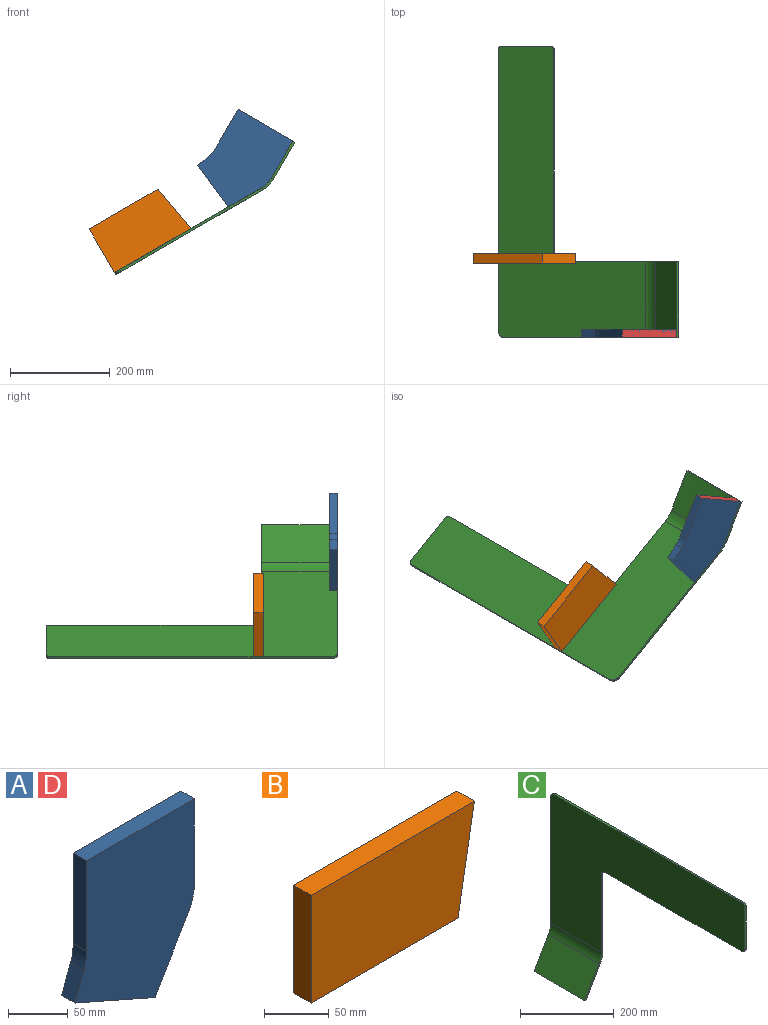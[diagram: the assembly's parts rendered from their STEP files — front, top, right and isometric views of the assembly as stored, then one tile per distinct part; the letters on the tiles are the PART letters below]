
ASSEMBLY  parts=4 mates=9
PART A: 11 faces, bbox 140.6x15.9x179.9 mm
  f0: plane 179.9x140.62mm, normal (0,-1,0), area 19853.6mm2, adj f2,f3,f4,f5,f6,f7,f8,f9
  f1: plane 179.9x140.62mm, normal (0,1,0), area 19853.6mm2, adj f2,f3,f4,f5,f6,f7,f8,f9
  f2: plane 92.5x15.88mm, normal (-1,0,0), area 1468.4mm2, adj f0,f1,f4,f10
  f3: plane 89.68x15.88mm, normal (1,0,0), area 1423.6mm2, adj f0,f1,f4,f5
  f4: plane 127x15.88mm, normal (0,0,1), area 2016.1mm2, adj f0,f1,f2,f3
  f5: cylinder r=42.03mm len=15.88mm, axis (0,-1,0), area 193.9mm2, adj f0,f1,f3,f7
  f6: plane 67.98x39.7mm, normal (0.86,0,-0.5), area 1249.7mm2, adj f0,f1,f7,f9
  f7: cylinder r=40.32mm len=15.88mm, axis (0,-1,0), area 177.7mm2, adj f0,f1,f5,f6
  f8: plane 28.24x15.88mm, normal (-0.94,0,0.35), area 478.1mm2, adj f0,f1,f9,f10
  f9: plane 94.25x41.52mm, normal (-0.4,0,-0.92), area 1635mm2, adj f0,f1,f6,f8
  f10: cylinder r=50.8mm len=17.64mm, axis (0,1,0), area 286mm2, adj f0,f1,f2,f8
PART B: 6 faces, bbox 177.8x19.1x101.6 mm
  f0: plane 101.6x19.05mm, normal (-1,0,0), area 1935.5mm2, adj f1,f3,f4,f5
  f1: plane 159.89x19.05mm, normal (0,0,-1), area 3045.8mm2, adj f0,f2,f4,f5
  f2: plane 101.6x19.05mm, normal (0.98,0,-0.17), area 1965.3mm2, adj f1,f3,f4,f5
  f3: plane 177.8x19.05mm, normal (0,0,1), area 3387.1mm2, adj f0,f2,f4,f5
  f4: plane 177.8x101.6mm, normal (0,-1,0), area 17154.4mm2, adj f0,f1,f2,f3
  f5: plane 177.8x101.6mm, normal (0,1,0), area 17154.4mm2, adj f0,f1,f2,f3
PART C: 20 faces, bbox 54.9x584.2x444.9 mm
  f0: plane 565.15x4.76mm, normal (0,0,1), area 2691.5mm2, adj f1,f8,f9,f10
  f1: cylinder r=12.7mm len=12.7mm, axis (1,0,0), area 95mm2, adj f0,f2,f9,f10
  f2: plane 329.29x4.76mm, normal (0,1,0), area 1568.2mm2, adj f1,f9,f10,f16
  f3: plane 202.29x4.76mm, normal (0,-1,0), area 963.4mm2, adj f4,f9,f10,f17
  f4: cylinder r=12.7mm len=12.7mm, axis (1,0,0), area 95mm2, adj f3,f5,f9,f10
  f5: plane 412.75x4.76mm, normal (0,0,-1), area 1965.7mm2, adj f4,f6,f9,f10
  f6: cylinder r=6.35mm len=6.35mm, axis (1,0,0), area 47.5mm2, adj f5,f7,f9,f10
  f7: plane 114.3x4.76mm, normal (0,-1,0), area 544.4mm2, adj f6,f8,f9,f10
  f8: cylinder r=6.35mm len=6.35mm, axis (1,0,0), area 47.5mm2, adj f0,f7,f9,f10
  f9: plane 584.2x341.99mm, normal (-1,0,0), area 106940.3mm2, adj f0,f1,f2,f3,f4,f5,f6,f7
  f10: plane 584.2x341.99mm, normal (1,0,0), area 106940.3mm2, adj f0,f1,f2,f3,f4,f5,f6,f7
  f11: plane 77.48x47.48mm, normal (0,-1,0), area 413mm2, adj f13,f14,f15,f17
  f12: plane 77.48x47.48mm, normal (0,1,0), area 413mm2, adj f13,f14,f15,f16
  f13: plane 152.4x4.12mm, normal (-0.5,0,-0.87), area 725.8mm2, adj f11,f12,f14,f15
  f14: plane 152.4x75.1mm, normal (-0.87,0,0.5), area 13214.9mm2, adj f11,f12,f13,f19
  f15: plane 152.4x75.1mm, normal (0.87,0,-0.5), area 13214.9mm2, adj f11,f12,f13,f18
  f16: plane 27.78x11.57mm, normal (0,1,0), area 132.6mm2, adj f2,f12,f18,f19
  f17: plane 27.78x11.57mm, normal (0,-1,0), area 132.6mm2, adj f3,f11,f18,f19
  f18: cylinder r=55.56mm len=152.4mm, axis (0,1,0), area 4433.7mm2, adj f10,f15,f16,f17
  f19: cylinder r=50.8mm len=152.4mm, axis (0,1,0), area 4053.7mm2, adj f9,f14,f16,f17
PART D: same geometry as A
PLACE A rot(axis=(0,1,0),30deg) t=(-130.82,-331.8,301.88)mm
PLACE B rot(axis=(-0.97,0,-0.26),180deg) t=(-478.27,-198.45,138.09)mm
PLACE C rot(axis=(-0.87,0,0.5),180deg) t=(-324.44,16.95,136.28)mm
PLACE D rot(axis=(0,1,0),30deg) t=(-130.82,-331.8,301.88)mm
MATE planar C.f13 <-> A.f4  axis (0.5,0,0.87) through (-122.77,-271.47,308.25)mm
MATE planar C.f14 <-> A.f3  axis (-0.87,0,0.5) through (-146.51,-271.47,271.9)mm
MATE planar C.f14 <-> D.f3  axis (-0.87,0,0.5) through (-146.51,-271.47,271.9)mm
MATE planar C.f9 <-> B.f3  axis (-0.5,0,0.87) through (-382.55,-121.72,102.73)mm
MATE planar D.f0 <-> C.f12  axis (0,-1,0) through (-221.81,-347.67,274.23)mm
MATE planar D.f4 <-> C.f13  axis (0.5,0,0.87) through (-179.82,-339.74,341.2)mm
MATE planar B.f0 <-> C.f0  axis (-0.87,0,-0.5) through (-508.35,-188.92,88.76)mm
MATE planar C.f2 <-> A.f0  axis (0,-1,0) through (-328.18,-347.67,131.37)mm
MATE planar A.f1 <-> C.f11  axis (0,1,0) through (-221.81,-331.8,274.23)mm
